# Revit family: Power-ModularDevices-GEWISS-90AM-MOTOR_PROTECTION
name_source: partatom
category: Apparecchi elettrici
revit_build: Autodesk Revit 2016 (Build: 20161004_0715(x64)
units: mm (PartAtom-declared; Revit-internal decimal feet)

## family parameters
Condiviso = No
Host = Superficie
Mantenere orientamento annotazione = Sì
Numero OmniClass = 23.80.50.00
Punto di calcolo locali = Sì
Quota connettore circolare = Usa diametro
Taglio con vuoti quando caricato = No
Tipo di parte = Normale
Titolo OmniClass = Terminals for Power Supply

## types (13) — shared parameters
Catalogue = POWER
Catalogue Range = 90 AM
Electrocod = 1751
IDF = be284e65-0030-41ab-a52b-3de678b45daf
IDT = 9a90badc-123e-4117-a2a4-f62144c76397
Immagine tipo = GW96751.jpg
No. Chorus modules = 3
No. of modules EN 50022 = 3
No. of poles = 3P
Number of poles = 3P
Numero di poli = 1
Produttore = GEWISS S.p.A.
Prospetto di default = 1219 mm
Rated voltage = 230/400ac
Rated voltage (V) = 230/400 ac
SEO = Motor switch
Spostamento_x = -340 mm
Technical sheet = https://www.gewiss.com
URL = https://www.gewiss.com
Version file RFA = 18.0
carico = Altro
potenza in watt = 0 V

## per-type parameters (varying)
| type | Descrizione | EAN code | Modello | Operating current |
| GW96753 - MOTOR PROTECTION SWITCH 0.25-0.4A | MOTOR PROTECTION SWITCH 0.25-0.4A | 8011564184336 | GW96753 | 0,25-0,4A |
| GW96752 - MOTOR PROTECTION SWITCH 0.16-0.25A | MOTOR PROTECTION SWITCH 0.16-0.25A | 8011564184329 | GW96752 | 0,16-0,25A |
| GW96755 - MOTOR PROTECTION SWITCH 0.63-1A | MOTOR PROTECTION SWITCH 0.63-1A | 8011564184428 | GW96755 | 0,63-1A |
| GW96756 - MOTOR PROTECTION SWITCH 1-1.6A | MOTOR PROTECTION SWITCH 1-1.6A | 8011564184435 | GW96756 | 1-1,6A |
| GW96761 - MOTOR PROTECTION SWITCH 10-16A | MOTOR PROTECTION SWITCH 10-16A | 8011564184503 | GW96761 | 10-16A |
| GW96757 - MOTOR PROTECTION SWITCH 1.6-2.5A | MOTOR PROTECTION SWITCH 1.6-2.5A | 8011564184442 | GW96757 | 1,6-2,5A |
| GW96762 - MOTOR PROTECTION SWITCH 16-25A | MOTOR PROTECTION SWITCH 16-25A | 8011564184510 | GW96762 | 16-25A |
| GW96751 - MOTOR PROTECTION SWITCH 0.1-0.16A | MOTOR PROTECTION SWITCH 0.1-0.16A | 8011564184312 | GW96751 | 0,1-0,16A |
| GW96758 - MOTOR PROTECTION SWITCH 2.5-4A | MOTOR PROTECTION SWITCH 2.5-4A | 8011564184459 | GW96758 | 2,5-4A |
| GW96760 - MOTOR PROTECTION SWITCH 6.3-10A | MOTOR PROTECTION SWITCH 6.3-10A | 8011564184497 | GW96760 | 6,3-10A |
| GW96754 - MOTOR PROTECTION SWITCH 0.4-0.63A | MOTOR PROTECTION SWITCH 0.4-0.63A | 8011564184411 | GW96754 | 0,4-0,63A |
| GW96763 - MOTOR PROTECTION SWITCH 25-40A | MOTOR PROTECTION SWITCH 25-40A | 8011564184527 | GW96763 | 25-40A |
| GW96759 - MOTOR PROTECTION SWITCH 4-6.3A | MOTOR PROTECTION SWITCH 4-6.3A | 8011564184473 | GW96759 | 4-6,3A |
